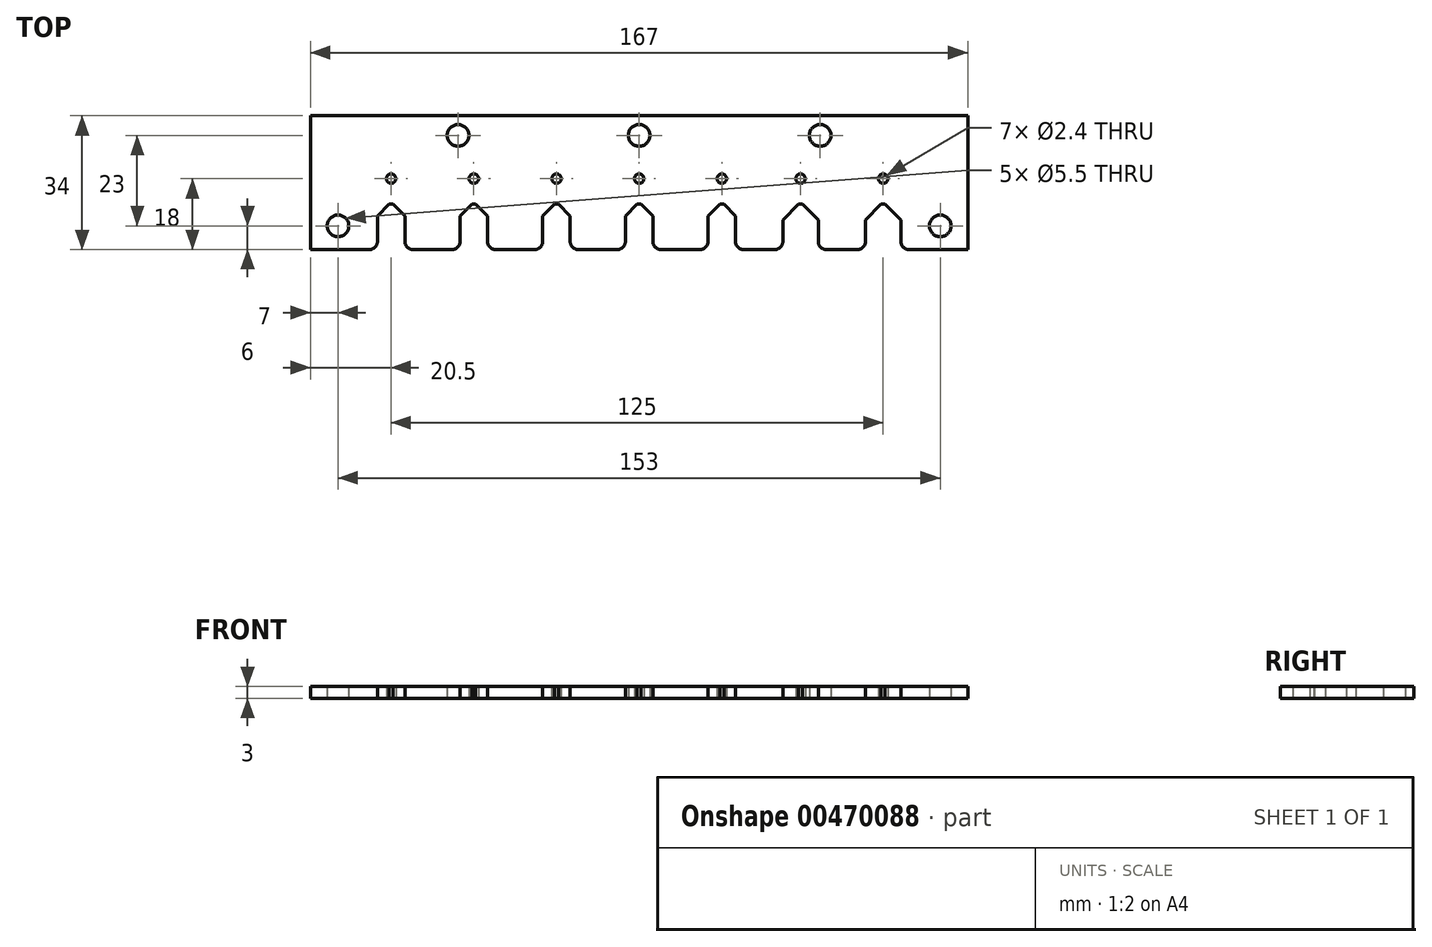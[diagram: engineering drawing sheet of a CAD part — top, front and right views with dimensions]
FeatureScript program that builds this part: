
annotation { "Feature Type Name" : "Feature", "Feature Type Description" : "" }
export const myFeature = defineFeature(function(context is Context, id is Id, definition is map)
    precondition{}
    {
        {
            var Q0;
            Q0=qCreatedBy(makeId("Top.planeOp"),FACE);
            var sketch = newSketch(context, id + "F0", { "sketchPlane" : qUnion([Q0])});
            skLineSegment(sketch, "E0", {"start": v(0, 0) * mm, "end": v(0, 34) * mm});
            skLineSegment(sketch, "E1", {"start": v(0, 34) * mm, "end": v(167, 34) * mm});
            skLineSegment(sketch, "E2", {"start": v(167, 34) * mm, "end": v(167, 0) * mm});
            skLineSegment(sketch, "E3", {"start": v(167, 0) * mm, "end": v(152, 0) * mm});
            skLineSegment(sketch, "E4", {"start": v(150, 2) * mm, "end": v(150, 8) * mm});
            skLineSegment(sketch, "E5", {"start": v(146, 12) * mm, "end": v(145, 12) * mm});
            skLineSegment(sketch, "E6", {"start": v(141, 8) * mm, "end": v(141, 2) * mm});
            skLineSegment(sketch, "E7", {"start": v(139, 0) * mm, "end": v(131, 0) * mm});
            skLineSegment(sketch, "E8", {"start": v(129, 2) * mm, "end": v(129, 8) * mm});
            skLineSegment(sketch, "E9", {"start": v(125, 12) * mm, "end": v(124, 12) * mm});
            skLineSegment(sketch, "E10", {"start": v(120, 8) * mm, "end": v(120, 2) * mm});
            skLineSegment(sketch, "E11", {"start": v(118, 0) * mm, "end": v(110, 0) * mm});
            skLineSegment(sketch, "E12", {"start": v(108, 2) * mm, "end": v(108, 9) * mm});
            skLineSegment(sketch, "E13", {"start": v(105, 12) * mm, "end": v(104, 12) * mm});
            skLineSegment(sketch, "E14", {"start": v(101, 9) * mm, "end": v(101, 2) * mm});
            skLineSegment(sketch, "E15", {"start": v(99, 0) * mm, "end": v(89, 0) * mm});
            skLineSegment(sketch, "E16", {"start": v(87, 2) * mm, "end": v(87, 9) * mm});
            skLineSegment(sketch, "E17", {"start": v(84, 12) * mm, "end": v(83, 12) * mm});
            skLineSegment(sketch, "E18", {"start": v(80, 9) * mm, "end": v(80, 2) * mm});
            skLineSegment(sketch, "E19", {"start": v(78, 0) * mm, "end": v(68, 0) * mm});
            skLineSegment(sketch, "E20", {"start": v(66, 2) * mm, "end": v(66, 9) * mm});
            skLineSegment(sketch, "E21", {"start": v(63, 12) * mm, "end": v(62, 12) * mm});
            skLineSegment(sketch, "E22", {"start": v(59, 9) * mm, "end": v(59, 2) * mm});
            skLineSegment(sketch, "E23", {"start": v(57, 0) * mm, "end": v(47, 0) * mm});
            skLineSegment(sketch, "E24", {"start": v(45, 2) * mm, "end": v(45, 9) * mm});
            skLineSegment(sketch, "E25", {"start": v(42, 12) * mm, "end": v(41, 12) * mm});
            skLineSegment(sketch, "E26", {"start": v(38, 9) * mm, "end": v(38, 2) * mm});
            skLineSegment(sketch, "E27", {"start": v(36, 0) * mm, "end": v(26, 0) * mm});
            skLineSegment(sketch, "E28", {"start": v(24, 2) * mm, "end": v(24, 9) * mm});
            skLineSegment(sketch, "E29", {"start": v(21, 12) * mm, "end": v(20, 12) * mm});
            skLineSegment(sketch, "E30", {"start": v(17, 9) * mm, "end": v(17, 2) * mm});
            skLineSegment(sketch, "E31", {"start": v(15, 0) * mm, "end": v(0, 0) * mm});
            skCircle(sketch, "E32", {"center": v(160, 6) * mm, "radius": 2.75 * mm});
            skCircle(sketch, "E33", {"center": v(129.5, 29) * mm, "radius": 2.75 * mm});
            skCircle(sketch, "E34", {"center": v(37.5, 29) * mm, "radius": 2.75 * mm});
            skPoint(sketch, "E35.centerSnap0", {"position": v(20.5, 12) * mm});
            skCircle(sketch, "E36", {"center": v(20.5, 9) * mm, "radius": 3 * mm, "construction": true});
            skLineSegment(sketch, "E37", {"start": v(20.5, 12) * mm, "end": v(20.5, 0) * mm, "construction": true});
            skCircle(sketch, "E38", {"center": v(20.5, 9) * mm, "radius": 5 * mm, "construction": true});
            skCircle(sketch, "E39", {"center": v(41.5, 9) * mm, "radius": 3 * mm, "construction": true});
            skPoint(sketch, "E39.centerSnap0", {"position": v(41.5, 12) * mm});
            skCircle(sketch, "E40", {"center": v(41.5, 9) * mm, "radius": 5 * mm, "construction": true});
            skPoint(sketch, "E41.visualSharp", {"position": v(17, 0) * mm});
            skArc(sketch, "E41.filletArc", {"start": v(15, 0) * mm, "mid": v(16.41, 0.59) * mm, "end": v(17, 2) * mm});
            skPoint(sketch, "E42.visualSharp", {"position": v(24, 0) * mm});
            skArc(sketch, "E42.filletArc", {"start": v(24, 2) * mm, "mid": v(24.59, 0.59) * mm, "end": v(26, 0) * mm});
            skPoint(sketch, "E43.visualSharp", {"position": v(38, 0) * mm});
            skArc(sketch, "E43.filletArc", {"start": v(36, 0) * mm, "mid": v(37.41, 0.59) * mm, "end": v(38, 2) * mm});
            skPoint(sketch, "E44.visualSharp", {"position": v(45, 0) * mm});
            skArc(sketch, "E44.filletArc", {"start": v(45, 2) * mm, "mid": v(45.59, 0.59) * mm, "end": v(47, 0) * mm});
            skPoint(sketch, "E45.visualSharp", {"position": v(59, 0) * mm});
            skArc(sketch, "E45.filletArc", {"start": v(57, 0) * mm, "mid": v(58.41, 0.59) * mm, "end": v(59, 2) * mm});
            skPoint(sketch, "E46.visualSharp", {"position": v(66, 0) * mm});
            skArc(sketch, "E46.filletArc", {"start": v(66, 2) * mm, "mid": v(66.59, 0.59) * mm, "end": v(68, 0) * mm});
            skPoint(sketch, "E47.visualSharp", {"position": v(80, 0) * mm});
            skArc(sketch, "E47.filletArc", {"start": v(78, 0) * mm, "mid": v(79.41, 0.59) * mm, "end": v(80, 2) * mm});
            skPoint(sketch, "E48.visualSharp", {"position": v(87, 0) * mm});
            skArc(sketch, "E48.filletArc", {"start": v(87, 2) * mm, "mid": v(87.59, 0.59) * mm, "end": v(89, 0) * mm});
            skPoint(sketch, "E49.visualSharp", {"position": v(101, 0) * mm});
            skArc(sketch, "E49.filletArc", {"start": v(99, 0) * mm, "mid": v(100.41, 0.59) * mm, "end": v(101, 2) * mm});
            skPoint(sketch, "E50.visualSharp", {"position": v(108, 0) * mm});
            skArc(sketch, "E50.filletArc", {"start": v(108, 2) * mm, "mid": v(108.59, 0.59) * mm, "end": v(110, 0) * mm});
            skPoint(sketch, "E51.visualSharp", {"position": v(120, 0) * mm});
            skArc(sketch, "E51.filletArc", {"start": v(118, 0) * mm, "mid": v(119.41, 0.59) * mm, "end": v(120, 2) * mm});
            skPoint(sketch, "E52.visualSharp", {"position": v(129, 0) * mm});
            skArc(sketch, "E52.filletArc", {"start": v(129, 2) * mm, "mid": v(129.59, 0.59) * mm, "end": v(131, 0) * mm});
            skPoint(sketch, "E53.visualSharp", {"position": v(141, 0) * mm});
            skArc(sketch, "E53.filletArc", {"start": v(139, 0) * mm, "mid": v(140.41, 0.59) * mm, "end": v(141, 2) * mm});
            skPoint(sketch, "E54.visualSharp", {"position": v(150, 0) * mm});
            skArc(sketch, "E54.filletArc", {"start": v(150, 2) * mm, "mid": v(150.59, 0.59) * mm, "end": v(152, 0) * mm});
            skCircle(sketch, "E55", {"center": v(7, 6) * mm, "radius": 2.75 * mm});
            skPoint(sketch, "E56.visualSharp", {"position": v(45, 12) * mm});
            skArc(sketch, "E56.filletArc", {"start": v(45, 9) * mm, "mid": v(44.12, 11.12) * mm, "end": v(42, 12) * mm});
            skPoint(sketch, "E57.visualSharp", {"position": v(38, 12) * mm});
            skArc(sketch, "E57.filletArc", {"start": v(41, 12) * mm, "mid": v(38.88, 11.12) * mm, "end": v(38, 9) * mm});
            skPoint(sketch, "E58.visualSharp", {"position": v(24, 12) * mm});
            skArc(sketch, "E58.filletArc", {"start": v(24, 9) * mm, "mid": v(23.12, 11.12) * mm, "end": v(21, 12) * mm});
            skPoint(sketch, "E59.visualSharp", {"position": v(17, 12) * mm});
            skArc(sketch, "E59.filletArc", {"start": v(20, 12) * mm, "mid": v(17.88, 11.12) * mm, "end": v(17, 9) * mm});
            skPoint(sketch, "E60.visualSharp", {"position": v(59, 12) * mm});
            skArc(sketch, "E60.filletArc", {"start": v(62, 12) * mm, "mid": v(59.88, 11.12) * mm, "end": v(59, 9) * mm});
            skPoint(sketch, "E61.visualSharp", {"position": v(66, 12) * mm});
            skArc(sketch, "E61.filletArc", {"start": v(66, 9) * mm, "mid": v(65.12, 11.12) * mm, "end": v(63, 12) * mm});
            skPoint(sketch, "E62.visualSharp", {"position": v(80, 12) * mm});
            skArc(sketch, "E62.filletArc", {"start": v(83, 12) * mm, "mid": v(80.88, 11.12) * mm, "end": v(80, 9) * mm});
            skPoint(sketch, "E63.visualSharp", {"position": v(87, 12) * mm});
            skArc(sketch, "E63.filletArc", {"start": v(87, 9) * mm, "mid": v(86.12, 11.12) * mm, "end": v(84, 12) * mm});
            skPoint(sketch, "E64.visualSharp", {"position": v(101, 12) * mm});
            skArc(sketch, "E64.filletArc", {"start": v(104, 12) * mm, "mid": v(101.88, 11.12) * mm, "end": v(101, 9) * mm});
            skPoint(sketch, "E65.visualSharp", {"position": v(108, 12) * mm});
            skArc(sketch, "E65.filletArc", {"start": v(108, 9) * mm, "mid": v(107.12, 11.12) * mm, "end": v(105, 12) * mm});
            skPoint(sketch, "E66", {"position": v(62.5, 12) * mm});
            skPoint(sketch, "E67", {"position": v(83.5, 12) * mm});
            skCircle(sketch, "E68", {"center": v(83.5, 9) * mm, "radius": 3 * mm, "construction": true});
            skCircle(sketch, "E69", {"center": v(83.5, 9) * mm, "radius": 5 * mm, "construction": true});
            skCircle(sketch, "E70", {"center": v(62.5, 9) * mm, "radius": 3 * mm, "construction": true});
            skCircle(sketch, "E71", {"center": v(62.5, 9) * mm, "radius": 5 * mm, "construction": true});
            skPoint(sketch, "E72", {"position": v(104.5, 12) * mm});
            skCircle(sketch, "E73", {"center": v(104.5, 9) * mm, "radius": 3 * mm, "construction": true});
            skCircle(sketch, "E74", {"center": v(104.5, 9) * mm, "radius": 5 * mm, "construction": true});
            skCircle(sketch, "E75", {"center": v(145.5, 9) * mm, "radius": 3 * mm, "construction": true});
            skCircle(sketch, "E76", {"center": v(145.5, 9) * mm, "radius": 7 * mm, "construction": true});
            skPoint(sketch, "E77.visualSharp", {"position": v(141, 12) * mm});
            skArc(sketch, "E77.filletArc", {"start": v(145, 12) * mm, "mid": v(142.17, 10.83) * mm, "end": v(141, 8) * mm});
            skPoint(sketch, "E78.visualSharp", {"position": v(150, 12) * mm});
            skArc(sketch, "E78.filletArc", {"start": v(150, 8) * mm, "mid": v(148.83, 10.83) * mm, "end": v(146, 12) * mm});
            skPoint(sketch, "E79.visualSharp", {"position": v(129, 12) * mm});
            skArc(sketch, "E79.filletArc", {"start": v(129, 8) * mm, "mid": v(127.83, 10.83) * mm, "end": v(125, 12) * mm});
            skPoint(sketch, "E80.visualSharp", {"position": v(120, 12) * mm});
            skArc(sketch, "E80.filletArc", {"start": v(124, 12) * mm, "mid": v(121.17, 10.83) * mm, "end": v(120, 8) * mm});
            skPoint(sketch, "E81", {"position": v(145.5, 12) * mm});
            skCircle(sketch, "E82", {"center": v(124.5, 9) * mm, "radius": 3 * mm, "construction": true});
            skPoint(sketch, "E82.centerSnap0", {"position": v(124.5, 12) * mm});
            skCircle(sketch, "E83", {"center": v(124.5, 9) * mm, "radius": 7 * mm, "construction": true});
            skCircle(sketch, "E84", {"center": v(20.5, 18) * mm, "radius": 1.2 * mm});
            skLineSegment(sketch, "E85", {"start": v(20.5, 12) * mm, "end": v(20.5, 34) * mm, "construction": true});
            skCircle(sketch, "E86.1.0.0", {"center": v(41.5, 18) * mm, "radius": 1.2 * mm});
            skCircle(sketch, "E86.2.0.0", {"center": v(62.5, 18) * mm, "radius": 1.2 * mm});
            skCircle(sketch, "E86.3.0.0", {"center": v(83.5, 18) * mm, "radius": 1.2 * mm});
            skCircle(sketch, "E86.4.0.0", {"center": v(104.5, 18) * mm, "radius": 1.2 * mm});
            skLineSegment(sketch, "E86.direction1", {"start": v(20.5, 18) * mm, "end": v(41.5, 18) * mm, "construction": true});
            skCircle(sketch, "E87.1.0.0", {"center": v(124.5, 18) * mm, "radius": 1.2 * mm});
            skLineSegment(sketch, "E87.direction1", {"start": v(104.5, 18) * mm, "end": v(124.5, 18) * mm, "construction": true});
            skCircle(sketch, "E88.1.0.0", {"center": v(145.5, 18) * mm, "radius": 1.2 * mm});
            skLineSegment(sketch, "E88.direction1", {"start": v(124.5, 18) * mm, "end": v(145.5, 18) * mm, "construction": true});
            skLineSegment(sketch, "E89", {"start": v(83.5, 34) * mm, "end": v(83.5, 24.65) * mm, "construction": true});
            skCircle(sketch, "E90", {"center": v(83.5, 29) * mm, "radius": 2.75 * mm});
            skLineSegment(sketch, "E91", {"start": v(20.5, 12) * mm, "end": v(17, 8.5) * mm});
            skLineSegment(sketch, "E92", {"start": v(20.5, 12) * mm, "end": v(24, 8.5) * mm});
            skLineSegment(sketch, "E93", {"start": v(20, 11.5) * mm, "end": v(21, 11.5) * mm});
            skLineSegment(sketch, "E94.1.0.0", {"start": v(41.5, 12) * mm, "end": v(38, 8.5) * mm});
            skLineSegment(sketch, "E94.1.0.1", {"start": v(41, 11.5) * mm, "end": v(42, 11.5) * mm});
            skLineSegment(sketch, "E94.1.0.2", {"start": v(41.5, 12) * mm, "end": v(45, 8.5) * mm});
            skLineSegment(sketch, "E94.2.0.0", {"start": v(62.5, 12) * mm, "end": v(59, 8.5) * mm});
            skLineSegment(sketch, "E94.2.0.1", {"start": v(62, 11.5) * mm, "end": v(63, 11.5) * mm});
            skLineSegment(sketch, "E94.2.0.2", {"start": v(62.5, 12) * mm, "end": v(66, 8.5) * mm});
            skLineSegment(sketch, "E94.3.0.0", {"start": v(83.5, 12) * mm, "end": v(80, 8.5) * mm});
            skLineSegment(sketch, "E94.3.0.1", {"start": v(83, 11.5) * mm, "end": v(84, 11.5) * mm});
            skLineSegment(sketch, "E94.3.0.2", {"start": v(83.5, 12) * mm, "end": v(87, 8.5) * mm});
            skLineSegment(sketch, "E94.4.0.0", {"start": v(104.5, 12) * mm, "end": v(101, 8.5) * mm});
            skLineSegment(sketch, "E94.4.0.1", {"start": v(104, 11.5) * mm, "end": v(105, 11.5) * mm});
            skLineSegment(sketch, "E94.4.0.2", {"start": v(104.5, 12) * mm, "end": v(108, 8.5) * mm});
            skLineSegment(sketch, "E94.direction1", {"start": v(17, 8.5) * mm, "end": v(38, 8.5) * mm, "construction": true});
            skLineSegment(sketch, "E95", {"start": v(124.5, 12) * mm, "end": v(120, 7.5) * mm});
            skLineSegment(sketch, "E96", {"start": v(124.5, 12) * mm, "end": v(129, 7.5) * mm});
            skLineSegment(sketch, "E97", {"start": v(124, 11.5) * mm, "end": v(125, 11.5) * mm});
            skLineSegment(sketch, "E98.1.0.0", {"start": v(145.5, 12) * mm, "end": v(141, 7.5) * mm});
            skLineSegment(sketch, "E98.1.0.1", {"start": v(145.5, 12) * mm, "end": v(150, 7.5) * mm});
            skLineSegment(sketch, "E98.1.0.2", {"start": v(145, 11.5) * mm, "end": v(146, 11.5) * mm});
            skLineSegment(sketch, "E98.direction1", {"start": v(120, 7.5) * mm, "end": v(141, 7.5) * mm, "construction": true});
            skSolve(sketch);
        }
        {
            var Q0;
            {var subQ4=sQuery(id+"F0.wireOp",EDGE,"E64.filletArc");Q0=makeQuery(id+"F0.imprint","IMPRINT",FACE,{"disambiguationData":[TD([[makeQuery(id+"F0.imprint","IMPRINT",EDGE,{"derivedFrom":subQ4}),1.0]])]});}
            var Q1;
            {var subQ4=sQuery(id+"F0.wireOp",EDGE,"E65.filletArc");Q1=makeQuery(id+"F0.imprint","IMPRINT",FACE,{"disambiguationData":[TD([[makeQuery(id+"F0.imprint","IMPRINT",EDGE,{"derivedFrom":subQ4}),1.0]])]});}
            var Q2;
            {var subQ3=sQuery(id+"F0.wireOp",EDGE,"E94.4.0.1");Q2=makeQuery(id+"F0.imprint","IMPRINT",FACE,{"disambiguationData":[TD([[makeQuery(id+"F0.imprint","IMPRINT",EDGE,{"derivedFrom":subQ3}),1.0]])]});}
            var Q3;
            Q3=makeQuery(id+"F0.imprint","IMPRINT",FACE,{"disambiguationData":[TD([[makeQuery(id+"F0.imprint","IMPRINT",EDGE,{"derivedFrom":sQuery(id+"F0.wireOp",EDGE,"E0")}),-1.0]])]});
            var Q4;
            {var subQ0=sQuery(id+"F0.wireOp",EDGE,"E78.filletArc");Q4=makeQuery(id+"F0.imprint","IMPRINT",FACE,{"disambiguationData":[TD([[makeQuery(id+"F0.imprint","IMPRINT",EDGE,{"derivedFrom":subQ0}),1.0]])]});}
            var Q5;
            {var subQ3=sQuery(id+"F0.wireOp",EDGE,"E98.1.0.2");Q5=makeQuery(id+"F0.imprint","IMPRINT",FACE,{"disambiguationData":[TD([[makeQuery(id+"F0.imprint","IMPRINT",EDGE,{"derivedFrom":subQ3}),1.0]])]});}
            var Q6;
            {var subQ0=sQuery(id+"F0.wireOp",EDGE,"E77.filletArc");Q6=makeQuery(id+"F0.imprint","IMPRINT",FACE,{"disambiguationData":[TD([[makeQuery(id+"F0.imprint","IMPRINT",EDGE,{"derivedFrom":subQ0}),1.0]])]});}
            var Q7;
            {var subQ4=sQuery(id+"F0.wireOp",EDGE,"E79.filletArc");Q7=makeQuery(id+"F0.imprint","IMPRINT",FACE,{"disambiguationData":[TD([[makeQuery(id+"F0.imprint","IMPRINT",EDGE,{"derivedFrom":subQ4}),1.0]])]});}
            var Q8;
            {var subQ3=sQuery(id+"F0.wireOp",EDGE,"E97");Q8=makeQuery(id+"F0.imprint","IMPRINT",FACE,{"disambiguationData":[TD([[makeQuery(id+"F0.imprint","IMPRINT",EDGE,{"derivedFrom":subQ3}),1.0]])]});}
            var Q9;
            {var subQ4=sQuery(id+"F0.wireOp",EDGE,"E80.filletArc");Q9=makeQuery(id+"F0.imprint","IMPRINT",FACE,{"disambiguationData":[TD([[makeQuery(id+"F0.imprint","IMPRINT",EDGE,{"derivedFrom":subQ4}),1.0]])]});}
            var Q10;
            {var subQ0=sQuery(id+"F0.wireOp",EDGE,"E63.filletArc");Q10=makeQuery(id+"F0.imprint","IMPRINT",FACE,{"disambiguationData":[TD([[makeQuery(id+"F0.imprint","IMPRINT",EDGE,{"derivedFrom":subQ0}),1.0]])]});}
            var Q11;
            {var subQ3=sQuery(id+"F0.wireOp",EDGE,"E94.3.0.1");Q11=makeQuery(id+"F0.imprint","IMPRINT",FACE,{"disambiguationData":[TD([[makeQuery(id+"F0.imprint","IMPRINT",EDGE,{"derivedFrom":subQ3}),1.0]])]});}
            var Q12;
            {var subQ0=sQuery(id+"F0.wireOp",EDGE,"E62.filletArc");Q12=makeQuery(id+"F0.imprint","IMPRINT",FACE,{"disambiguationData":[TD([[makeQuery(id+"F0.imprint","IMPRINT",EDGE,{"derivedFrom":subQ0}),1.0]])]});}
            var Q13;
            {var subQ4=sQuery(id+"F0.wireOp",EDGE,"E61.filletArc");Q13=makeQuery(id+"F0.imprint","IMPRINT",FACE,{"disambiguationData":[TD([[makeQuery(id+"F0.imprint","IMPRINT",EDGE,{"derivedFrom":subQ4}),1.0]])]});}
            var Q14;
            {var subQ3=sQuery(id+"F0.wireOp",EDGE,"E94.2.0.1");Q14=makeQuery(id+"F0.imprint","IMPRINT",FACE,{"disambiguationData":[TD([[makeQuery(id+"F0.imprint","IMPRINT",EDGE,{"derivedFrom":subQ3}),1.0]])]});}
            var Q15;
            {var subQ4=sQuery(id+"F0.wireOp",EDGE,"E60.filletArc");Q15=makeQuery(id+"F0.imprint","IMPRINT",FACE,{"disambiguationData":[TD([[makeQuery(id+"F0.imprint","IMPRINT",EDGE,{"derivedFrom":subQ4}),1.0]])]});}
            var Q16;
            {var subQ4=sQuery(id+"F0.wireOp",EDGE,"E56.filletArc");Q16=makeQuery(id+"F0.imprint","IMPRINT",FACE,{"disambiguationData":[TD([[makeQuery(id+"F0.imprint","IMPRINT",EDGE,{"derivedFrom":subQ4}),1.0]])]});}
            var Q17;
            {var subQ3=sQuery(id+"F0.wireOp",EDGE,"E94.1.0.1");Q17=makeQuery(id+"F0.imprint","IMPRINT",FACE,{"disambiguationData":[TD([[makeQuery(id+"F0.imprint","IMPRINT",EDGE,{"derivedFrom":subQ3}),1.0]])]});}
            var Q18;
            {var subQ4=sQuery(id+"F0.wireOp",EDGE,"E57.filletArc");Q18=makeQuery(id+"F0.imprint","IMPRINT",FACE,{"disambiguationData":[TD([[makeQuery(id+"F0.imprint","IMPRINT",EDGE,{"derivedFrom":subQ4}),1.0]])]});}
            var Q19;
            {var subQ4=sQuery(id+"F0.wireOp",EDGE,"E58.filletArc");Q19=makeQuery(id+"F0.imprint","IMPRINT",FACE,{"disambiguationData":[TD([[makeQuery(id+"F0.imprint","IMPRINT",EDGE,{"derivedFrom":subQ4}),1.0]])]});}
            var Q20;
            {var subQ3=sQuery(id+"F0.wireOp",EDGE,"E93");Q20=makeQuery(id+"F0.imprint","IMPRINT",FACE,{"disambiguationData":[TD([[makeQuery(id+"F0.imprint","IMPRINT",EDGE,{"derivedFrom":subQ3}),1.0]])]});}
            var Q21;
            {var subQ4=sQuery(id+"F0.wireOp",EDGE,"E59.filletArc");Q21=makeQuery(id+"F0.imprint","IMPRINT",FACE,{"disambiguationData":[TD([[makeQuery(id+"F0.imprint","IMPRINT",EDGE,{"derivedFrom":subQ4}),1.0]])]});}
            extrude(context, id + "F1", {"entities" : qUnion([Q0, Q1, Q2, Q3, Q4, Q5, Q6, Q7, Q8, Q9, Q10, Q11, Q12, Q13, Q14, Q15, Q16, Q17, Q18, Q19, Q20, Q21]), "offsetDistance" : 25 * mm, "depth" : 3 * mm});
        }
    });
